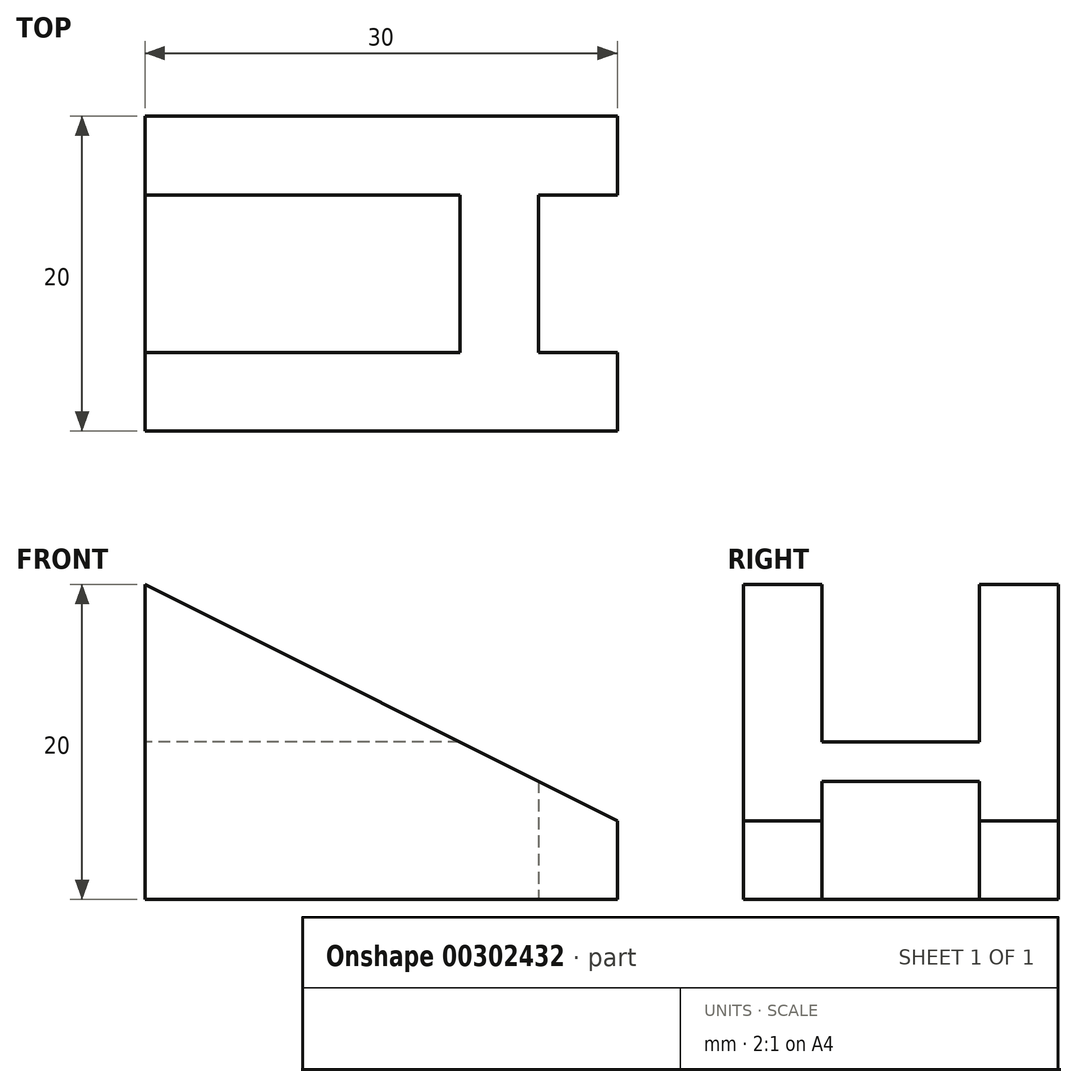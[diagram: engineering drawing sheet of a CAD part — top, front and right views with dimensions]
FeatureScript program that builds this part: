
annotation { "Feature Type Name" : "Feature", "Feature Type Description" : "" }
export const myFeature = defineFeature(function(context is Context, id is Id, definition is map)
    precondition{}
    {
        {
            var Q0;
            Q0=qCreatedBy(makeId("Front.planeOp"),FACE);
            var sketch = newSketch(context, id + "F0", { "sketchPlane" : qUnion([Q0])});
            skLineSegment(sketch, "E0", {"start": v(0, 0) * mm, "end": v(0, 20) * mm});
            skLineSegment(sketch, "E1", {"start": v(0, 20) * mm, "end": v(30, 5) * mm});
            skLineSegment(sketch, "E2", {"start": v(30, 5) * mm, "end": v(30, 0) * mm});
            skLineSegment(sketch, "E3", {"start": v(30, 0) * mm, "end": v(0, 0) * mm});
            skSolve(sketch);
        }
        {
            var Q0;
            Q0 = qSketchRegion(id + "F0", true);
            extrude(context, id + "F1", {"entities" : qUnion([Q0]), "depth" : 20 * mm});
        }
        {
            var Q0;
            Q0=qCreatedBy(makeId("Right.planeOp"),FACE);
            var sketch = newSketch(context, id + "F2", { "sketchPlane" : qUnion([Q0])});
            skLineSegment(sketch, "E4", {"start": v(-5, 20) * mm, "end": v(-5, 10) * mm});
            skLineSegment(sketch, "E5", {"start": v(-5, 10) * mm, "end": v(-15, 10) * mm});
            skLineSegment(sketch, "E6", {"start": v(-15, 10) * mm, "end": v(-15, 20) * mm});
            skLineSegment(sketch, "E7", {"start": v(0, 20) * mm, "end": v(-20, 20) * mm});
            skLineSegment(sketch, "E8", {"start": v(-20, 20) * mm, "end": v(-20, 0) * mm});
            skLineSegment(sketch, "E9", {"start": v(-20, 0) * mm, "end": v(0, 0) * mm});
            skLineSegment(sketch, "E10", {"start": v(0, 0) * mm, "end": v(0, 20) * mm});
            skSolve(sketch);
        }
        {
            var Q0;
            {var subQ0=sQuery(id+"F2.wireOp",EDGE,"E4");Q0=makeQuery(id+"F2.imprint","IMPRINT",FACE,{"disambiguationData":[TD([[makeQuery(id+"F2.imprint","IMPRINT",EDGE,{"derivedFrom":subQ0}),-1.0]])]});}
            extrude(context, id + "F3", {"entities" : qUnion([Q0]), "operationType" : NewBodyOperationType.REMOVE, "depth" : 25 * mm});
        }
        {
            var Q0;
            Q0=makeQuery(id+"F1.opExtrude","SWEPT_FACE",FACE,{"disambiguationData":[OSD([sQuery(id+"F0.wireOp",EDGE,"E3")])]});
            var sketch = newSketch(context, id + "F4", { "sketchPlane" : qUnion([Q0])});
            skLineSegment(sketch, "E11", {"start": v(30, 15) * mm, "end": v(25, 15) * mm});
            skLineSegment(sketch, "E12", {"start": v(25, 15) * mm, "end": v(25, 5) * mm});
            skLineSegment(sketch, "E13", {"start": v(25, 5) * mm, "end": v(30, 5) * mm});
            skLineSegment(sketch, "E14", {"start": v(30, 5) * mm, "end": v(30, 15) * mm});
            skSolve(sketch);
        }
        {
            var Q0;
            Q0=makeQuery(id+"F4.imprint","IMPRINT",FACE,{"disambiguationData":[TD([[makeQuery(id+"F4.imprint","IMPRINT",EDGE,{"derivedFrom":sQuery(id+"F4.wireOp",EDGE,"E11")}),1.0]])]});
            extrude(context, id + "F5", {"entities" : qUnion([Q0]), "operationType" : NewBodyOperationType.REMOVE, "oppositeDirection" : true, "depth" : 25 * mm});
        }
    });
